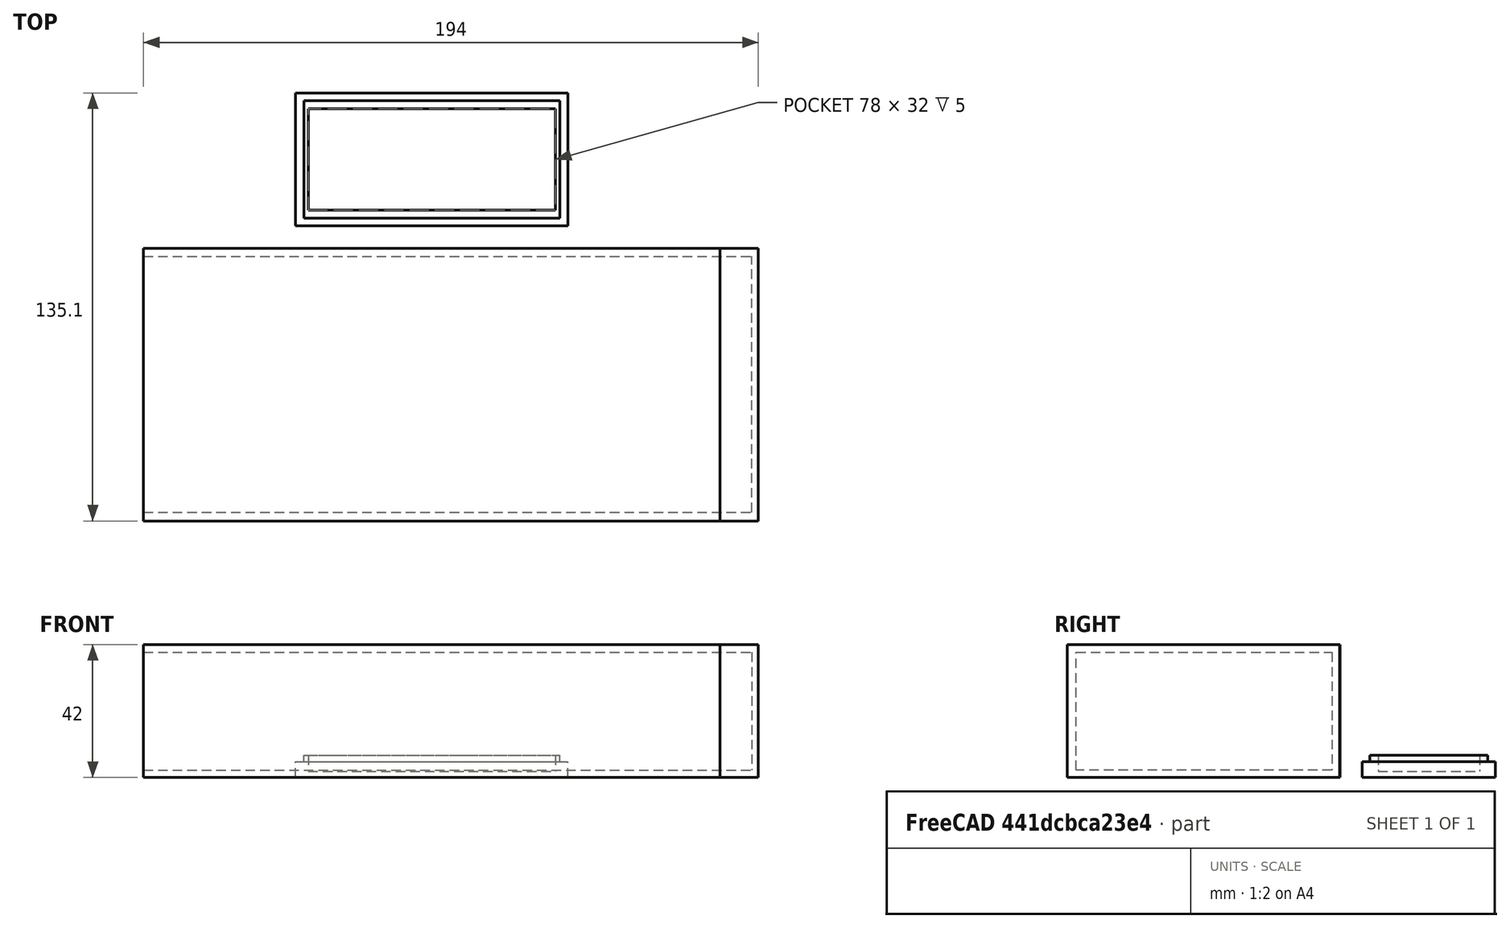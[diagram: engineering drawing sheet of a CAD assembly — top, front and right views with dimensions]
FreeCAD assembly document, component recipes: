
FREECAD ASSEMBLY — COMPONENT RECIPES ("pylon_w_power")

This assembly document has 2 components, labeled P0..P1 below (a component is one placed body or linked part). 2 of them carry a construction recipe — the FreeCAD feature program that regenerates the part from scratch, quoted from this document or its linked companion documents; the rest are supplied as boundary geometry only. No exploded tour is included for this assembly.
COMPONENT P0 — recipe-attached ("Body001", modeled in this document).
Construction recipe (the document's own serialized feature program — sketch geometry with constraints, then the solid features built on it; lengths are millimeters unless a unit is written):

FEATURE [Sketcher::SketchObject] Sketch010
  ArcFitTolerance = 1e-06
  AttachmentSupport = -> [XY_Plane008]
  FullyConstrained = false
  MakeInternals = false
  MapMode = 5
  sketch-geometry (5):
    g0: LineSegment StartX=-43 StartY=50.1027 StartZ=0 EndX=43 EndY=50.1027 EndZ=0
    g1: LineSegment StartX=43 StartY=50.1027 StartZ=0 EndX=43 EndY=92.1027 EndZ=0
    g2: LineSegment StartX=43 StartY=92.1027 StartZ=0 EndX=-43 EndY=92.1027 EndZ=0
    g3: LineSegment StartX=-43 StartY=92.1027 StartZ=0 EndX=-43 EndY=50.1027 EndZ=0
    g4: GeomPoint [constr] X=0 Y=71.1027 Z=0
  constraints (12):
    c: Coincident(g0,g1)
    c: Coincident(g1,g2)
    c: Coincident(g2,g3)
    c: Coincident(g3,g0)
    c: Horizontal(g0)
    c: Horizontal(g2)
    c: Vertical(g1)
    c: Vertical(g3)
    c: Symmetric(g2,g0,g4)
    c: Distance(g1,g3) = 86
    c: Distance(g0,g2) = 42
    c: PointOnObject(g4,g-2)
FEATURE [PartDesign::Pad] Pad004
  Direction = (0,0,1)
  Length = 5
  Length2 = 10
  Profile = -> Sketch010
  ReferenceAxis = -> Sketch010 [N_Axis]
  Refine = true
  Suppressed = false
  Type = 0
FEATURE [Sketcher::SketchObject] Sketch012
  ArcFitTolerance = 1e-06
  AttachmentSupport = -> [Pad004]
  FullyConstrained = false
  MakeInternals = false
  MapMode = 5
  Placement = pos=(0,0,5) rot=(0,0,1;0rad)
  sketch-geometry (5):
    g0: LineSegment StartX=-40.365 StartY=52.5172 StartZ=0 EndX=40.365 EndY=52.5172 EndZ=0
    g1: LineSegment StartX=40.365 StartY=52.5172 StartZ=0 EndX=40.365 EndY=89.6872 EndZ=0
    g2: LineSegment StartX=40.365 StartY=89.6872 StartZ=0 EndX=-40.365 EndY=89.6872 EndZ=0
    g3: LineSegment StartX=-40.365 StartY=89.6872 StartZ=0 EndX=-40.365 EndY=52.5172 EndZ=0
    g4: GeomPoint [constr] X=0 Y=71.1022 Z=0
  constraints (12):
    c: Coincident(g0,g1)
    c: Coincident(g1,g2)
    c: Coincident(g2,g3)
    c: Coincident(g3,g0)
    c: Horizontal(g0)
    c: Horizontal(g2)
    c: Vertical(g1)
    c: Vertical(g3)
    c: Symmetric(g2,g0,g4)
    c: Distance(g1,g3) = 80.73
    c: Distance(g0,g2) = 37.17
    c: PointOnObject(g4,g-2)
FEATURE [PartDesign::Pad] Pad005
  BaseFeature = -> Pad004
  Direction = (0,0,1)
  Length = 2
  Length2 = 10
  Profile = -> Sketch012
  ReferenceAxis = -> Sketch012 [N_Axis]
  Refine = true
  Suppressed = false
  Type = 0
FEATURE [Sketcher::SketchObject] Sketch013
  ArcFitTolerance = 1e-06
  AttachmentSupport = -> [Pad005]
  FullyConstrained = false
  MakeInternals = false
  MapMode = 5
  Placement = pos=(0,0,7) rot=(0,0,1;0rad)
  sketch-geometry (5):
    g0: LineSegment StartX=-39 StartY=55.0963 StartZ=0 EndX=39 EndY=55.0963 EndZ=0
    g1: LineSegment StartX=39 StartY=55.0963 StartZ=0 EndX=39 EndY=87.0963 EndZ=0
    g2: LineSegment StartX=39 StartY=87.0963 StartZ=0 EndX=-39 EndY=87.0963 EndZ=0
    g3: LineSegment StartX=-39 StartY=87.0963 StartZ=0 EndX=-39 EndY=55.0963 EndZ=0
    g4: GeomPoint [constr] X=0 Y=71.0963 Z=0
  constraints (12):
    c: Coincident(g0,g1)
    c: Coincident(g1,g2)
    c: Coincident(g2,g3)
    c: Coincident(g3,g0)
    c: Horizontal(g0)
    c: Horizontal(g2)
    c: Vertical(g1)
    c: Vertical(g3)
    c: Symmetric(g2,g0,g4)
    c: Distance(g1,g3) = 78
    c: Distance(g0,g2) = 32
    c: PointOnObject(g4,g-2)
FEATURE [PartDesign::Pocket] Pocket006
  BaseFeature = -> Pad005
  Direction = (0,0,-1)
  Length = 5
  Length2 = 5
  Profile = -> Sketch013
  ReferenceAxis = -> Sketch013 [N_Axis]
  Refine = true
  Suppressed = false
  Type = 0
FEATURE [PartDesign::Body] Body001
  AllowCompound = false
  Group = -> [Sketch010,Pad004,Sketch012,Pad005,Sketch013,Pocket006]
  Origin = -> Origin008
  Tip = -> Pocket006
COMPONENT P1 — recipe-attached ("Part", modeled in this document).
Construction recipe (the document's own serialized feature program — sketch geometry with constraints, then the solid features built on it; lengths are millimeters unless a unit is written):

FEATURE [Sketcher::SketchObject] Sketch
  ArcFitTolerance = 1e-06
  AttachmentSupport = -> [XY_Plane]
  FullyConstrained = true
  MakeInternals = false
  MapMode = 5
  sketch-geometry (5):
    g0: LineSegment StartX=-91 StartY=-43 StartZ=0 EndX=91 EndY=-43 EndZ=0
    g1: LineSegment StartX=91 StartY=-43 StartZ=0 EndX=91 EndY=43 EndZ=0
    g2: LineSegment StartX=91 StartY=43 StartZ=0 EndX=-91 EndY=43 EndZ=0
    g3: LineSegment StartX=-91 StartY=43 StartZ=0 EndX=-91 EndY=-43 EndZ=0
    g4: GeomPoint [constr] X=0 Y=0 Z=0
  constraints (12):
    c: Coincident(g0,g1)
    c: Coincident(g1,g2)
    c: Coincident(g2,g3)
    c: Coincident(g3,g0)
    c: Horizontal(g0)
    c: Horizontal(g2)
    c: Vertical(g1)
    c: Vertical(g3)
    c: Symmetric(g2,g0,g4)
    c: Distance(g1,g3) = 182
    c: Distance(g0,g2) = 86
    c: Coincident(g4,g-1)
FEATURE [PartDesign::Pad] Pad
  Direction = (0,0,1)
  Length = 42
  Length2 = 10
  Profile = -> Sketch
  ReferenceAxis = -> Sketch [N_Axis]
  Refine = true
  Suppressed = false
  Type = 0
FEATURE [Sketcher::SketchObject] Sketch001
  ArcFitTolerance = 1e-06
  AttachmentSupport = -> [YZ_Plane]
  FullyConstrained = true
  MakeInternals = false
  MapMode = 5
  Placement = pos=(0,0,0) rot=(0.57735,0.57735,0.57735;2.0944rad)
FEATURE [Sketcher::SketchObject] Sketch002
  ArcFitTolerance = 1e-06
  AttachmentSupport = -> [Pad]
  FullyConstrained = false
  MakeInternals = false
  MapMode = 5
  Placement = pos=(-91,0,0) rot=(0.57735,-0.57735,-0.57735;2.0944rad)
  sketch-geometry (5):
    g0: LineSegment StartX=-38 StartY=4.98784 StartZ=0 EndX=38 EndY=4.98784 EndZ=0
    g1: LineSegment StartX=38 StartY=4.98784 StartZ=0 EndX=38 EndY=36.9878 EndZ=0
    g2: LineSegment StartX=38 StartY=36.9878 StartZ=0 EndX=-38 EndY=36.9878 EndZ=0
    g3: LineSegment StartX=-38 StartY=36.9878 StartZ=0 EndX=-38 EndY=4.98784 EndZ=0
    g4: GeomPoint [constr] X=1e-16 Y=20.9878 Z=0
  constraints (12):
    c: Coincident(g0,g1)
    c: Coincident(g1,g2)
    c: Coincident(g2,g3)
    c: Coincident(g3,g0)
    c: Horizontal(g0)
    c: Horizontal(g2)
    c: Vertical(g1)
    c: Vertical(g3)
    c: Symmetric(g2,g0,g4)
    c: Distance(g1,g3) = 76
    c: Distance(g0,g2) = 32
    c: PointOnObject(g4,g-2)
FEATURE [PartDesign::Pocket] Pocket
  BaseFeature = -> Pad
  Direction = (1,0,0)
  Length = 172
  Length2 = 5
  Profile = -> Sketch002
  ReferenceAxis = -> Sketch002 [N_Axis]
  Refine = true
  Suppressed = false
  Type = 0
FEATURE [Sketcher::SketchObject] Sketch003
  ArcFitTolerance = 1e-06
  AttachmentSupport = -> [XY_Plane]
  FullyConstrained = true
  MakeInternals = false
  MapMode = 5
FEATURE [Sketcher::SketchObject] Sketch007
  ArcFitTolerance = 1e-06
  AttachmentSupport = -> [Pocket]
  FullyConstrained = false
  MakeInternals = false
  MapMode = 5
  Placement = pos=(91,0,0) rot=(0.57735,0.57735,0.57735;2.0944rad)
  sketch-geometry (4):
    g0: LineSegment StartX=-42.9997 StartY=41.9991 StartZ=0 EndX=-42.9997 EndY=0 EndZ=0
    g1: LineSegment StartX=-42.9997 StartY=0 StartZ=0 EndX=42.9974 EndY=0 EndZ=0
    g2: LineSegment StartX=42.9974 StartY=0 StartZ=0 EndX=42.9974 EndY=41.9991 EndZ=0
    g3: LineSegment StartX=42.9974 StartY=41.9991 StartZ=0 EndX=-42.9997 EndY=41.9991 EndZ=0
  constraints (9):
    c: Coincident(g0,g1)
    c: Coincident(g1,g2)
    c: Coincident(g2,g3)
    c: Coincident(g3,g0)
    c: Vertical(g0)
    c: Vertical(g2)
    c: Horizontal(g1)
    c: Horizontal(g3)
    c: PointOnObject(g1,g-1)
FEATURE [PartDesign::Pad] Pad003
  BaseFeature = -> Pocket
  Direction = (1,0,0)
  Length = 12
  Length2 = 10
  Profile = -> Sketch007
  ReferenceAxis = -> Sketch007 [N_Axis]
  Refine = true
  Suppressed = false
  Type = 0
FEATURE [Sketcher::SketchObject] Sketch008
  ArcFitTolerance = 1e-06
  AttachmentSupport = -> [Pad003]
  FullyConstrained = false
  MakeInternals = false
  MapMode = 5
  Placement = pos=(81,0,0) rot=(0.57735,-0.57735,-0.57735;2.0944rad)
  sketch-geometry (4):
    g0: LineSegment StartX=-37.8741 StartY=36.8036 StartZ=0 EndX=-37.8741 EndY=5.03903 EndZ=0
    g1: LineSegment StartX=-37.8741 StartY=5.03903 StartZ=0 EndX=37.9514 EndY=5.03903 EndZ=0
    g2: LineSegment StartX=37.9514 StartY=5.03903 StartZ=0 EndX=37.9514 EndY=36.8036 EndZ=0
    g3: LineSegment StartX=37.9514 StartY=36.8036 StartZ=0 EndX=-37.8741 EndY=36.8036 EndZ=0
  constraints (8):
    c: Coincident(g0,g1)
    c: Coincident(g1,g2)
    c: Coincident(g2,g3)
    c: Coincident(g3,g0)
    c: Vertical(g0)
    c: Vertical(g2)
    c: Horizontal(g1)
    c: Horizontal(g3)
FEATURE [PartDesign::Pocket] Pocket002
  BaseFeature = -> Pad003
  Direction = (1,0,0)
  Length = 15
  Length2 = 5
  Profile = -> Sketch008
  ReferenceAxis = -> Sketch008 [N_Axis]
  Refine = true
  Suppressed = false
  Type = 0
FEATURE [Sketcher::SketchObject] Sketch009
  ArcFitTolerance = 1e-06
  AttachmentSupport = -> [Pocket002]
  FullyConstrained = false
  MakeInternals = false
  MapMode = 5
  Placement = pos=(-91,0,0) rot=(0.57735,-0.57735,-0.57735;2.0944rad)
  sketch-geometry (4):
    g0: LineSegment StartX=-40.5195 StartY=39.5025 StartZ=0 EndX=-40.5195 EndY=2.32773 EndZ=0
    g1: LineSegment StartX=-40.5195 StartY=2.32773 StartZ=0 EndX=40.2057 EndY=2.32773 EndZ=0
    g2: LineSegment StartX=40.2057 StartY=2.32773 StartZ=0 EndX=40.2057 EndY=39.5025 EndZ=0
    g3: LineSegment StartX=40.2057 StartY=39.5025 StartZ=0 EndX=-40.5195 EndY=39.5025 EndZ=0
  constraints (8):
    c: Coincident(g0,g1)
    c: Coincident(g1,g2)
    c: Coincident(g2,g3)
    c: Coincident(g3,g0)
    c: Vertical(g0)
    c: Vertical(g2)
    c: Horizontal(g1)
    c: Horizontal(g3)
FEATURE [PartDesign::Pocket] Pocket003
  BaseFeature = -> Pocket002
  Direction = (1,0,0)
  Length = 187
  Length2 = 5
  Profile = -> Sketch009
  ReferenceAxis = -> Sketch009 [N_Axis]
  Refine = true
  Suppressed = false
  Type = 0
FEATURE [PartDesign::Pocket] Pocket004
  BaseFeature = -> Pocket003
  Direction = (-1,0,0)
  Length = 4
  Length2 = 5
  Profile = -> Pocket003 [Edge31,Edge26,Edge30,Edge28]
  Refine = true
  Suppressed = false
  Type = 0
FEATURE [PartDesign::Pocket] Pocket005
  BaseFeature = -> Pocket004
  Direction = (1,0,0)
  Length = 5
  Length2 = 5
  Profile = -> Pocket004 [Face12]
  Refine = true
  Suppressed = false
  Type = 0
FEATURE [PartDesign::Body] Body
  AllowCompound = false
  Group = -> [Sketch,Pad,Sketch001,Sketch002,Pocket,Sketch003,Sketch007,Pad003,Sketch008,Pocket002,Sketch009,Pocket003,Pocket004,Pocket005]
  Origin = -> Origin
  Tip = -> Pocket005
PROVENANCE & LICENSES
A FreeCAD (.FCStd) document from a public repository crawl; recipes are the document's own serialized feature recipes (and, for linked parts, companion documents' recipes).
License: as declared in the source repository (recorded in the dataset sidecar).
